# Revit family: 500_Slenderline_Sliding_Window_OX_Standard
name_source: partatom
category: Windows
revit_build: Autodesk Revit 2014 (Build: 20130308_1515(x64)
units: mm (PartAtom-declared; Revit-internal decimal feet)

## types (33) — shared parameters
Centered In Wall = Yes
Custom Sash Width Left = 600 mm
Default Sill Height = 800 mm
Description = Slenderline Sliding Window
Equal Sash Width = Yes
Frame Thickness = 54 mm
Heavy Duty Interlocker = No
Limit Sash Height Max = 1500 mm  [stored 4.92126 ft]
Limit Sash Height Min = 300 mm  [stored 0.984252 ft]
Limit Sash Width Max = 750 mm  [stored 2.46063 ft]
Limit Sash Width Min = 300 mm  [stored 0.984252 ft]
Limit Window Height Min = 375 mm
Limit Window Width Min = 631 mm  [stored 2.07021 ft]
Manufacturer = Crealco
Model = 500
Rough Width = 3 mm  [stored 0.00984252 ft]
Sash Frame Seal = 1 mm  [stored 0.00328084 ft]
Standard Interlocker = Yes
URL = www.crealco.co.za
Wall Closure = By host
zero-valued in all types: Custom Frame Offset From Exterior, Is Heavy Duty Interlocker

## per-type parameters (varying)
| type | Area Left Sash Glazing | Area Right Sash Glazing | Clearvue SHGC Value | Clearvue U Value | Custom Windload | Custom Window Height | Custom Window Width | Energy Advantage SHGC Value | Energy Advantage U Value | Height | Intruderprufe LowE SHGC Value | Intruderprufe LowE U Value | Intruderprufe SHGC Value | Intruderprufe U Value | Limit Sash Width Left Max | Limit Sash Width Left Min | Limit Window Height Max | Limit Window Width Max | Max Pane Area | Sash Height | Sash Width Left | Sash Width Right | Width | Windload Design |
| 500SW-0906OX-1000Pa | 0.18 m² | 0.18 m² | 0.582 | 5.51 | 1000 mm  [stored 3.28084 ft] | 590 mm  [stored 1.9357 ft] | 890 mm  [stored 2.91995 ft] | 0.522 | 4.28 | 590 mm  [stored 1.9357 ft] | 0.442 | 4.18 | 0.553 | 5.39 | 559 mm  [stored 1.83399 ft] | 300 mm  [stored 0.984252 ft] | 1575 mm | 1531 mm  [stored 5.02297 ft] | 0.18 m² | 515 mm | 430 mm | 430 mm | 890 mm  [stored 2.91995 ft] | 1000 mm  [stored 3.28084 ft] |
| 500SW-1206OX-1000Pa | 0.24 m² | 0.24 m² | 0.593 | 5.7 | 1000 mm  [stored 3.28084 ft] | 590 mm  [stored 1.9357 ft] | 1190 mm  [stored 3.9042 ft] | 0.531 | 4.83 | 590 mm  [stored 1.9357 ft] | 0.45 | 4.32 | 0.563 | 5.57 | 750 mm  [stored 2.46063 ft] | 409 mm  [stored 1.34186 ft] | 1575 mm | 1531 mm  [stored 5.02297 ft] | 0.24 m² | 515 mm | 580 mm | 580 mm | 1190 mm  [stored 3.9042 ft] | 1000 mm  [stored 3.28084 ft] |
| 500SW-1506OX-1000Pa | 0.31 m² | 0.31 m² | 0.599 | 5.81 | 1000 mm  [stored 3.28084 ft] | 590 mm  [stored 1.9357 ft] | 1490 mm  [stored 4.88845 ft] | 0.536 | 4.44 | 590 mm  [stored 1.9357 ft] | 0.454 | 4.4 | 0.568 | 5.68 | 750 mm  [stored 2.46063 ft] | 709 mm  [stored 2.32612 ft] | 1575 mm | 1531 mm  [stored 5.02297 ft] | 0.31 m² | 515 mm | 730 mm | 730 mm | 1490 mm  [stored 4.88845 ft] | 1000 mm  [stored 3.28084 ft] |
| 500SW-0909OX-1000Pa | 0.3 m² | 0.3 m² | 0.655 | 5.38 | 1000 mm  [stored 3.28084 ft] | 890 mm  [stored 2.91995 ft] | 890 mm  [stored 2.91995 ft] | 0.586 | 3.99 | 890 mm  [stored 2.91995 ft] | 0.497 | 4.08 | 0.621 | 5.26 | 559 mm  [stored 1.83399 ft] | 300 mm  [stored 0.984252 ft] | 1575 mm | 1531 mm  [stored 5.02297 ft] | 0.3 m² | 815 mm | 430 mm | 430 mm | 890 mm  [stored 2.91995 ft] | 1000 mm  [stored 3.28084 ft] |
| 500SW-1209OX-1000Pa | 0.41 m² | 0.41 m² | 0.666 | 5.57 | 1000 mm  [stored 3.28084 ft] | 890 mm  [stored 2.91995 ft] | 1190 mm  [stored 3.9042 ft] | 0.596 | 4.08 | 890 mm  [stored 2.91995 ft] | 0.506 | 4.22 | 0.632 | 5.44 | 750 mm  [stored 2.46063 ft] | 409 mm  [stored 1.34186 ft] | 1575 mm | 1531 mm  [stored 5.02297 ft] | 0.41 m² | 815 mm | 580 mm | 580 mm | 1190 mm  [stored 3.9042 ft] | 1000 mm  [stored 3.28084 ft] |
| 500SW-1509OX-1000Pa | 0.52 m² | 0.52 m² | 0.673 | 5.68 | 1000 mm  [stored 3.28084 ft] | 890 mm  [stored 2.91995 ft] | 1490 mm  [stored 4.88845 ft] | 0.602 | 4.14 | 890 mm  [stored 2.91995 ft] | 0.51 | 4.3 | 0.639 | 5.55 | 750 mm  [stored 2.46063 ft] | 709 mm  [stored 2.32612 ft] | 1575 mm | 1531 mm  [stored 5.02297 ft] | 0.52 m² | 815 mm | 730 mm | 730 mm | 1490 mm  [stored 4.88845 ft] | 1000 mm  [stored 3.28084 ft] |
| 500SW-0912OX-1000Pa | 0.42 m² | 0.42 m² | 0.69 | 5.31 | 1000 mm  [stored 3.28084 ft] | 1190 mm  [stored 3.9042 ft] | 890 mm  [stored 2.91995 ft] | 0.617 | 3.85 | 1190 mm  [stored 3.9042 ft] | 0.524 | 4.02 | 0.655 | 5.19 | 559 mm  [stored 1.83399 ft] | 300 mm  [stored 0.984252 ft] | 1575 mm | 1531 mm  [stored 5.02297 ft] | 0.42 m² | 1115 mm | 430 mm | 430 mm | 890 mm  [stored 2.91995 ft] | 1000 mm  [stored 3.28084 ft] |
| 500SW-1212OX-1000Pa | 0.57 m² | 0.57 m² | 0.702 | 5.5 | 1000 mm  [stored 3.28084 ft] | 1190 mm  [stored 3.9042 ft] | 1190 mm  [stored 3.9042 ft] | 0.629 | 3.94 | 1190 mm  [stored 3.9042 ft] | 0.533 | 4.17 | 0.66 | 5.38 | 750 mm  [stored 2.46063 ft] | 409 mm  [stored 1.34186 ft] | 1575 mm | 1531 mm  [stored 5.02297 ft] | 0.57 m² | 1115 mm | 580 mm | 580 mm | 1190 mm  [stored 3.9042 ft] | 1000 mm  [stored 3.28084 ft] |
| 500SW-1512OX-1000Pa | 0.73 m² | 0.73 m² | 0.709 | 5.61 | 1000 mm  [stored 3.28084 ft] | 1190 mm  [stored 3.9042 ft] | 1490 mm  [stored 4.88845 ft] | 0.634 | 3.99 | 1190 mm  [stored 3.9042 ft] | 0.538 | 4.26 | 0.673 | 5.49 | 750 mm  [stored 2.46063 ft] | 709 mm  [stored 2.32612 ft] | 1575 mm | 1531 mm  [stored 5.02297 ft] | 0.73 m² | 1115 mm | 730 mm | 730 mm | 1490 mm  [stored 4.88845 ft] | 1000 mm  [stored 3.28084 ft] |
| 500SW-0915OX-1000Pa | 0.54 m² | 0.54 m² | 0.712 | 5.27 | 1000 mm  [stored 3.28084 ft] | 1490 mm  [stored 4.88845 ft] | 890 mm  [stored 2.91995 ft] | 0.636 | 3.77 | 1490 mm  [stored 4.88845 ft] | 0.54 | 3.99 | 0.675 | 5.15 | 559 mm  [stored 1.83399 ft] | 300 mm  [stored 0.984252 ft] | 1575 mm | 1531 mm  [stored 5.02297 ft] | 0.54 m² | 1415 mm | 430 mm | 430 mm | 890 mm  [stored 2.91995 ft] | 1000 mm  [stored 3.28084 ft] |
| 500SW-1215OX-1000Pa | 0.74 m² | 0.74 m² | 0.724 | 5.46 | 1000 mm  [stored 3.28084 ft] | 1490 mm  [stored 4.88845 ft] | 1190 mm  [stored 3.9042 ft] | 0.647 | 3.85 | 1490 mm  [stored 4.88845 ft] | 0.55 | 4.14 | 0.687 | 5.34 | 750 mm  [stored 2.46063 ft] | 409 mm  [stored 1.34186 ft] | 1575 mm | 1531 mm  [stored 5.02297 ft] | 0.74 m² | 1415 mm | 580 mm | 580 mm | 1190 mm  [stored 3.9042 ft] | 1000 mm  [stored 3.28084 ft] |
| 500SW-1515OX-1000Pa | 0.94 m² | 0.94 m² | 0.731 | 5.57 | 1000 mm  [stored 3.28084 ft] | 1490 mm  [stored 4.88845 ft] | 1490 mm  [stored 4.88845 ft] | 0.653 | 3.9 | 1490 mm  [stored 4.88845 ft] | 0.555 | 4.22 | 0.694 | 5.45 | 750 mm  [stored 2.46063 ft] | 709 mm  [stored 2.32612 ft] | 1575 mm | 1531 mm  [stored 5.02297 ft] | 0.94 m² | 1415 mm | 730 mm | 730 mm | 1490 mm  [stored 4.88845 ft] | 1000 mm  [stored 3.28084 ft] |
| 500SW-0906OX-1500Pa | 0.18 m² | 0.18 m² | 0.582 | 5.51 | 1500 mm  [stored 4.92126 ft] | 590 mm  [stored 1.9357 ft] | 890 mm  [stored 2.91995 ft] | 0.522 | 4.28 | 590 mm  [stored 1.9357 ft] | 0.442 | 4.18 | 0.553 | 5.39 | 559 mm  [stored 1.83399 ft] | 300 mm  [stored 0.984252 ft] | 1575 mm | 1531 mm  [stored 5.02297 ft] | 0.18 m² | 515 mm | 430 mm | 430 mm | 890 mm  [stored 2.91995 ft] | 1500 mm  [stored 4.92126 ft] |
| 500SW-0906OX-2000Pa | 0.18 m² | 0.18 m² | 0.582 | 5.51 | 2000 mm  [stored 6.56168 ft] | 590 mm  [stored 1.9357 ft] | 890 mm  [stored 2.91995 ft] | 0.522 | 4.28 | 590 mm  [stored 1.9357 ft] | 0.442 | 4.18 | 0.553 | 5.39 | 559 mm  [stored 1.83399 ft] | 300 mm  [stored 0.984252 ft] | 1575 mm | 1531 mm  [stored 5.02297 ft] | 0.18 m² | 515 mm | 430 mm | 430 mm | 890 mm  [stored 2.91995 ft] | 2000 mm  [stored 6.56168 ft] |
| 500SW-0909OX-1500Pa | 0.3 m² | 0.3 m² | 0.655 | 5.38 | 1500 mm  [stored 4.92126 ft] | 890 mm  [stored 2.91995 ft] | 890 mm  [stored 2.91995 ft] | 0.586 | 3.99 | 890 mm  [stored 2.91995 ft] | 0.497 | 4.08 | 0.621 | 5.26 | 559 mm  [stored 1.83399 ft] | 300 mm  [stored 0.984252 ft] | 1575 mm | 1531 mm  [stored 5.02297 ft] | 0.3 m² | 815 mm | 430 mm | 430 mm | 890 mm  [stored 2.91995 ft] | 1500 mm  [stored 4.92126 ft] |
| 500SW-0909OX-2000Pa | 0.3 m² | 0.3 m² | 0.655 | 5.38 | 2000 mm  [stored 6.56168 ft] | 890 mm  [stored 2.91995 ft] | 890 mm  [stored 2.91995 ft] | 0.586 | 3.99 | 890 mm  [stored 2.91995 ft] | 0.497 | 4.08 | 0.621 | 5.26 | 559 mm  [stored 1.83399 ft] | 300 mm  [stored 0.984252 ft] | 1575 mm | 1531 mm  [stored 5.02297 ft] | 0.3 m² | 815 mm | 430 mm | 430 mm | 890 mm  [stored 2.91995 ft] | 2000 mm  [stored 6.56168 ft] |
| 500SW-0912OX-1500Pa | 0.42 m² | 0.42 m² | 0.69 | 5.31 | 1500 mm  [stored 4.92126 ft] | 1190 mm  [stored 3.9042 ft] | 890 mm  [stored 2.91995 ft] | 0.617 | 3.85 | 1190 mm  [stored 3.9042 ft] | 0.524 | 4.02 | 0.655 | 5.19 | 559 mm  [stored 1.83399 ft] | 300 mm  [stored 0.984252 ft] | 1575 mm | 1531 mm  [stored 5.02297 ft] | 0.42 m² | 1115 mm | 430 mm | 430 mm | 890 mm  [stored 2.91995 ft] | 1500 mm  [stored 4.92126 ft] |
| 500SW-0912OX-2000Pa | 0.42 m² | 0.42 m² | 0.69 | 5.31 | 2000 mm  [stored 6.56168 ft] | 1190 mm  [stored 3.9042 ft] | 890 mm  [stored 2.91995 ft] | 0.617 | 3.85 | 1190 mm  [stored 3.9042 ft] | 0.524 | 4.02 | 0.655 | 5.19 | 559 mm  [stored 1.83399 ft] | 300 mm  [stored 0.984252 ft] | 1575 mm | 1531 mm  [stored 5.02297 ft] | 0.42 m² | 1115 mm | 430 mm | 430 mm | 890 mm  [stored 2.91995 ft] | 2000 mm  [stored 6.56168 ft] |
| 500SW-0915OX-1500Pa | 0.54 m² | 0.54 m² | 0.712 | 5.27 | 1500 mm  [stored 4.92126 ft] | 1490 mm  [stored 4.88845 ft] | 890 mm  [stored 2.91995 ft] | 0.636 | 3.77 | 1490 mm  [stored 4.88845 ft] | 0.54 | 3.99 | 0.675 | 5.15 | 559 mm  [stored 1.83399 ft] | 300 mm  [stored 0.984252 ft] | 1575 mm | 1531 mm  [stored 5.02297 ft] | 0.54 m² | 1415 mm | 430 mm | 430 mm | 890 mm  [stored 2.91995 ft] | 1500 mm  [stored 4.92126 ft] |
| 500SW-0915OX-2000Pa | 0.54 m² | 0.54 m² | 0.712 | 5.27 | 2000 mm  [stored 6.56168 ft] | 1490 mm  [stored 4.88845 ft] | 890 mm  [stored 2.91995 ft] | 0.636 | 3.77 | 1490 mm  [stored 4.88845 ft] | 0.54 | 3.99 | 0.675 | 5.15 | 559 mm  [stored 1.83399 ft] | 300 mm  [stored 0.984252 ft] | 1575 mm | 1531 mm  [stored 5.02297 ft] | 0.54 m² | 1415 mm | 430 mm | 430 mm | 890 mm  [stored 2.91995 ft] | 2000 mm  [stored 6.56168 ft] |
| 500SW-1206OX-1500Pa | 0.24 m² | 0.24 m² | 0.593 | 5.7 | 1500 mm  [stored 4.92126 ft] | 590 mm  [stored 1.9357 ft] | 1190 mm  [stored 3.9042 ft] | 0.531 | 4.83 | 590 mm  [stored 1.9357 ft] | 0.45 | 4.32 | 0.563 | 5.57 | 750 mm  [stored 2.46063 ft] | 409 mm  [stored 1.34186 ft] | 1575 mm | 1531 mm  [stored 5.02297 ft] | 0.24 m² | 515 mm | 580 mm | 580 mm | 1190 mm  [stored 3.9042 ft] | 1500 mm  [stored 4.92126 ft] |
| 500SW-1206OX-2000Pa | 0.24 m² | 0.24 m² | 0.593 | 5.7 | 2000 mm  [stored 6.56168 ft] | 590 mm  [stored 1.9357 ft] | 1190 mm  [stored 3.9042 ft] | 0.531 | 4.83 | 590 mm  [stored 1.9357 ft] | 0.45 | 4.32 | 0.563 | 5.57 | 750 mm  [stored 2.46063 ft] | 409 mm  [stored 1.34186 ft] | 1575 mm | 1531 mm  [stored 5.02297 ft] | 0.24 m² | 515 mm | 580 mm | 580 mm | 1190 mm  [stored 3.9042 ft] | 2000 mm  [stored 6.56168 ft] |
| 500SW-1209OX-1500Pa | 0.41 m² | 0.41 m² | 0.666 | 5.57 | 1500 mm  [stored 4.92126 ft] | 890 mm  [stored 2.91995 ft] | 1190 mm  [stored 3.9042 ft] | 0.596 | 4.08 | 890 mm  [stored 2.91995 ft] | 0.506 | 4.22 | 0.632 | 5.44 | 750 mm  [stored 2.46063 ft] | 409 mm  [stored 1.34186 ft] | 1575 mm | 1531 mm  [stored 5.02297 ft] | 0.41 m² | 815 mm | 580 mm | 580 mm | 1190 mm  [stored 3.9042 ft] | 1500 mm  [stored 4.92126 ft] |
| 500SW-1209OX-2000Pa | 0.41 m² | 0.41 m² | 0.666 | 5.57 | 2000 mm  [stored 6.56168 ft] | 890 mm  [stored 2.91995 ft] | 1190 mm  [stored 3.9042 ft] | 0.596 | 4.08 | 890 mm  [stored 2.91995 ft] | 0.506 | 4.22 | 0.632 | 5.44 | 750 mm  [stored 2.46063 ft] | 409 mm  [stored 1.34186 ft] | 1575 mm | 1531 mm  [stored 5.02297 ft] | 0.41 m² | 815 mm | 580 mm | 580 mm | 1190 mm  [stored 3.9042 ft] | 2000 mm  [stored 6.56168 ft] |
| 500SW-1212OX-1500Pa | 0.57 m² | 0.57 m² | 0.702 | 5.5 | 1500 mm  [stored 4.92126 ft] | 1190 mm  [stored 3.9042 ft] | 1190 mm  [stored 3.9042 ft] | 0.629 | 3.94 | 1190 mm  [stored 3.9042 ft] | 0.533 | 4.17 | 0.66 | 5.38 | 750 mm  [stored 2.46063 ft] | 409 mm  [stored 1.34186 ft] | 1575 mm | 1531 mm  [stored 5.02297 ft] | 0.57 m² | 1115 mm | 580 mm | 580 mm | 1190 mm  [stored 3.9042 ft] | 1500 mm  [stored 4.92126 ft] |
| 500SW-1212OX-2000Pa | 0.57 m² | 0.57 m² | 0.702 | 5.5 | 2000 mm  [stored 6.56168 ft] | 1190 mm  [stored 3.9042 ft] | 1190 mm  [stored 3.9042 ft] | 0.629 | 3.94 | 1190 mm  [stored 3.9042 ft] | 0.533 | 4.17 | 0.66 | 5.38 | 750 mm  [stored 2.46063 ft] | 409 mm  [stored 1.34186 ft] | 1575 mm | 1531 mm  [stored 5.02297 ft] | 0.57 m² | 1115 mm | 580 mm | 580 mm | 1190 mm  [stored 3.9042 ft] | 2000 mm  [stored 6.56168 ft] |
| 500SW-1215OX-1500Pa | 0.74 m² | 0.74 m² | 0.724 | 5.46 | 1500 mm  [stored 4.92126 ft] | 1490 mm  [stored 4.88845 ft] | 1190 mm  [stored 3.9042 ft] | 0.647 | 3.85 | 1490 mm  [stored 4.88845 ft] | 0.55 | 4.14 | 0.687 | 5.34 | 750 mm  [stored 2.46063 ft] | 409 mm  [stored 1.34186 ft] | 1575 mm | 1531 mm  [stored 5.02297 ft] | 0.74 m² | 1415 mm | 580 mm | 580 mm | 1190 mm  [stored 3.9042 ft] | 1500 mm  [stored 4.92126 ft] |
| 500SW-1215OX-2000Pa | 0.42 m² | 0.42 m² | 0.724 | 5.46 | 2000 mm  [stored 6.56168 ft] | 1490 mm  [stored 4.88845 ft] | 1190 mm  [stored 3.9042 ft] | 0.647 | 3.85 | 1190 mm  [stored 3.9042 ft] | 0.55 | 4.14 | 0.687 | 5.34 | 559 mm  [stored 1.83399 ft] | 300 mm  [stored 0.984252 ft] | 1190 mm  [stored 3.9042 ft] | 890 mm  [stored 2.91995 ft] | 0.42 m² | 1115 mm | 430 mm | 430 mm | 890 mm  [stored 2.91995 ft] | 2000 mm  [stored 6.56168 ft] |
| 500SW-1506OX-1500Pa | 0.31 m² | 0.31 m² | 0.599 | 5.81 | 1500 mm  [stored 4.92126 ft] | 590 mm  [stored 1.9357 ft] | 1490 mm  [stored 4.88845 ft] | 0.536 | 4.44 | 590 mm  [stored 1.9357 ft] | 0.454 | 4.4 | 0.568 | 5.68 | 750 mm  [stored 2.46063 ft] | 709 mm  [stored 2.32612 ft] | 1575 mm | 1531 mm  [stored 5.02297 ft] | 0.31 m² | 515 mm | 730 mm | 730 mm | 1490 mm  [stored 4.88845 ft] | 1500 mm  [stored 4.92126 ft] |
| 500SW-1506OX-2000Pa | 0.31 m² | 0.31 m² | 0.599 | 5.81 | 2000 mm  [stored 6.56168 ft] | 590 mm  [stored 1.9357 ft] | 1490 mm  [stored 4.88845 ft] | 0.536 | 4.44 | 590 mm  [stored 1.9357 ft] | 0.454 | 4.4 | 0.568 | 5.68 | 750 mm  [stored 2.46063 ft] | 709 mm  [stored 2.32612 ft] | 1575 mm | 1531 mm  [stored 5.02297 ft] | 0.31 m² | 515 mm | 730 mm | 730 mm | 1490 mm  [stored 4.88845 ft] | 2000 mm  [stored 6.56168 ft] |
| 500SW-1509OX-1500Pa | 0.52 m² | 0.52 m² | 0.673 | 5.68 | 1500 mm  [stored 4.92126 ft] | 890 mm  [stored 2.91995 ft] | 1490 mm  [stored 4.88845 ft] | 0.602 | 4.14 | 890 mm  [stored 2.91995 ft] | 0.51 | 4.3 | 0.639 | 5.55 | 750 mm  [stored 2.46063 ft] | 709 mm  [stored 2.32612 ft] | 1575 mm | 1531 mm  [stored 5.02297 ft] | 0.52 m² | 815 mm | 730 mm | 730 mm | 1490 mm  [stored 4.88845 ft] | 1500 mm  [stored 4.92126 ft] |
| 500SW-1509OX-2000Pa | 0.52 m² | 0.52 m² | 0.673 | 5.68 | 2000 mm  [stored 6.56168 ft] | 890 mm  [stored 2.91995 ft] | 1490 mm  [stored 4.88845 ft] | 0.602 | 4.14 | 890 mm  [stored 2.91995 ft] | 0.51 | 4.3 | 0.639 | 5.55 | 750 mm  [stored 2.46063 ft] | 709 mm  [stored 2.32612 ft] | 1575 mm | 1531 mm  [stored 5.02297 ft] | 0.52 m² | 815 mm | 730 mm | 730 mm | 1490 mm  [stored 4.88845 ft] | 2000 mm  [stored 6.56168 ft] |
| 500SW-1512OX-1500Pa | 0.73 m² | 0.73 m² | 0.709 | 5.61 | 1500 mm  [stored 4.92126 ft] | 1190 mm  [stored 3.9042 ft] | 1490 mm  [stored 4.88845 ft] | 0.634 | 3.99 | 1190 mm  [stored 3.9042 ft] | 0.538 | 4.26 | 0.673 | 5.49 | 750 mm  [stored 2.46063 ft] | 709 mm  [stored 2.32612 ft] | 1575 mm | 1531 mm  [stored 5.02297 ft] | 0.73 m² | 1115 mm | 730 mm | 730 mm | 1490 mm  [stored 4.88845 ft] | 1500 mm  [stored 4.92126 ft] |

note: [stored X ft] marks values corroborated as IEEE doubles in the binary element streams (Revit-internal decimal feet)

## geometry (parser evidence)
native form markers: Sweep x32
no freeform markers — native parametric forms only
